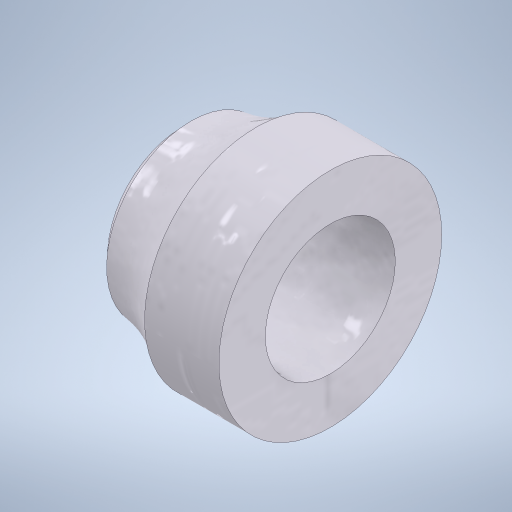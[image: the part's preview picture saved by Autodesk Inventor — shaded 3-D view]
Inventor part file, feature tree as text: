
AUTODESK INVENTOR PART (.ipt)
format: ipt  version: 2024 (Build 280153000, 153)  size: 291,840 bytes
history: native  units: mm
features: sketch x2, revolve x1, fillet x1, hole x1, chamfer x1
ambient origin geometry x8: Origin, YZ Plane, XZ Plane, XY Plane, X Axis, Y Axis, Z Axis, Center Point
bodies: Volumenkörper1 (feature_tree)
feature tree (6):
  revolve  "Umdrehung1"
  fillet  "Rundung1"  Radius=8.0mm
  hole  "Bohrung1"  [1 undecoded]
  chamfer  "Fasen1"  Angle=90.0deg  [1 undecoded]
  sketch  "Skizze1"  dims[d1=12.0mm d2=9.0mm]
  sketch  "Skizze2"  dims[d3=4.0mm d4=90.0deg d5=7.0mm d6=7.0mm d7=6.0mm d8=4.0mm d9=2.0mm d10=90.0deg d11=8.0mm d12=20.594885mm d13=0.5mm d14=2.0mm d15=45.0deg]
note: 2 required parameter values undecoded (feature->parameter linkage not recoverable at this tier; creation-order binding heuristic only, values carry confidence <= 0.55)
